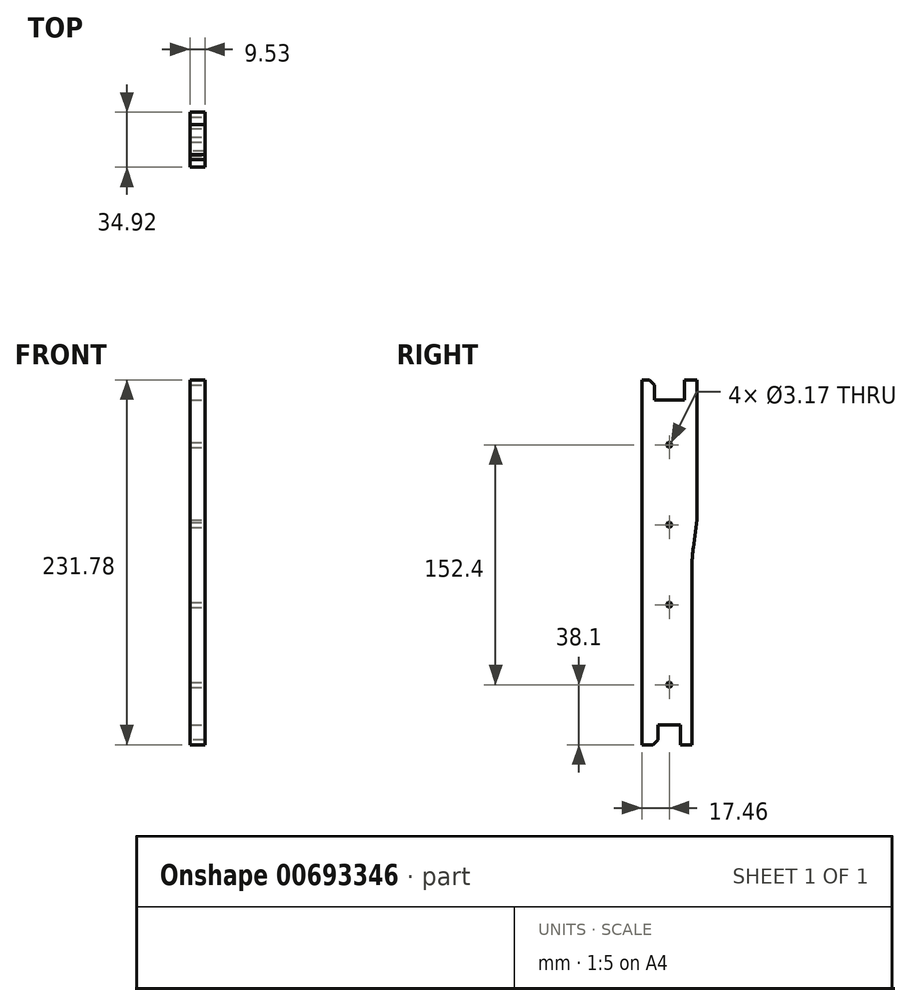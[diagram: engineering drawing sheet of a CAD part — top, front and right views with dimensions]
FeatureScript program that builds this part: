
annotation { "Feature Type Name" : "Feature", "Feature Type Description" : "" }
export const myFeature = defineFeature(function(context is Context, id is Id, definition is map)
    precondition{}
    {
        {
            var Q0;
            Q0=qCreatedBy(makeId("Right.planeOp"),FACE);
            var sketch = newSketch(context, id + "F0", { "sketchPlane" : qUnion([Q0])});
            skLineSegment(sketch, "E0.bottom", {"start": v(-17.46, 0) * mm, "end": v(17.46, 0) * mm});
            skLineSegment(sketch, "E0.top", {"start": v(-17.46, 231.78) * mm, "end": v(17.46, 231.78) * mm});
            skLineSegment(sketch, "E0.left", {"start": v(-17.46, 0) * mm, "end": v(-17.46, 231.78) * mm});
            skLineSegment(sketch, "E0.right", {"start": v(17.46, 0) * mm, "end": v(17.46, 231.78) * mm});
            skLineSegment(sketch, "E1", {"start": v(0, 0) * mm, "end": v(0, 231.78) * mm, "construction": true});
            skSolve(sketch);
        }
        {
            var Q0;
            Q0=qSketchRegion(id+"F0",true);
            extrude(context, id + "F1", {"entities" : qUnion([Q0]), "oppositeDirection" : true, "depth" : 9.52 * mm, "offsetDistance" : 25.4 * mm});
        }
        {
            var Q0;
            Q0=makeQuery(id+"F1.opExtrude","CAP_FACE",FACE,{"disambiguationData":[OSD([sQuery(id+"F0.wireOp",EDGE,"E0.bottom"),sQuery(id+"F0.wireOp",EDGE,"E0.top"),sQuery(id+"F0.wireOp",EDGE,"E0.left"),sQuery(id+"F0.wireOp",EDGE,"E0.right")])],"isStart":true});
            var sketch = newSketch(context, id + "F2", { "sketchPlane" : qUnion([Q0])});
            skLineSegment(sketch, "E2", {"start": v(14.29, 0) * mm, "end": v(14.29, 117.47) * mm});
            skLineSegment(sketch, "E3", {"start": v(14.29, 0) * mm, "end": v(17.46, 0) * mm});
            skLineSegment(sketch, "E4", {"start": v(0, 0) * mm, "end": v(0, 231.78) * mm, "construction": true});
            skLineSegment(sketch, "E5", {"start": v(14.29, 117.47) * mm, "end": v(17.46, 142.88) * mm});
            skLineSegment(sketch, "E6", {"start": v(17.46, 142.88) * mm, "end": v(17.46, 0) * mm});
            skSolve(sketch);
        }
        {
            var Q0;
            Q0=qSketchRegion(id+"F2",true);
            extrude(context, id + "F3", {"entities" : qUnion([Q0]), "operationType" : NewBodyOperationType.REMOVE, "endBound" : BoundingType.UP_TO_NEXT, "oppositeDirection" : true, "depth" : 25.4 * mm, "offsetDistance" : 25.4 * mm});
        }
        {
            var Q0;
            Q0=makeQuery(id+"F3.boolean.opBoolean","COPY",EDGE,{"derivedFrom":makeQuery(id+"F3.opExtrude","SWEPT_EDGE",EDGE,{"disambiguationData":[OSD([sQuery(id+"F2.wireOp",EDGE,"E2"),sQuery(id+"F2.wireOp",EDGE,"E5")])]})});
            var Q1;
            Q1=makeQuery(id+"F3.boolean.opBoolean","COPY",EDGE,{"derivedFrom":makeQuery(id+"F3.opExtrude","SWEPT_EDGE",EDGE,{"disambiguationData":[OSD([sQuery(id+"F0.wireOp",EDGE,"E0.right"),sQuery(id+"F2.wireOp",EDGE,"E5"),sQuery(id+"F2.wireOp",EDGE,"E6")])]})});
            fillet(context, id + "F4", {"entities" : qUnion([Q0, Q1]), "radius" : 127 * mm, "tangentPropagation" : true, "allowEdgeOverflow" : false});
        }
        {
            var Q0;
            Q0=makeQuery(id+"F1.opExtrude","CAP_FACE",FACE,{"disambiguationData":[OSD([sQuery(id+"F0.wireOp",EDGE,"E0.bottom"),sQuery(id+"F0.wireOp",EDGE,"E0.top"),sQuery(id+"F0.wireOp",EDGE,"E0.left"),sQuery(id+"F0.wireOp",EDGE,"E0.right")])],"isStart":true});
            var sketch = newSketch(context, id + "F5", { "sketchPlane" : qUnion([Q0])});
            skLineSegment(sketch, "E7", {"start": v(0, 231.78) * mm, "end": v(0, 202.75) * mm, "construction": true});
            skLineSegment(sketch, "E8.bottom", {"start": v(-9.53, 231.78) * mm, "end": v(9.53, 231.78) * mm});
            skLineSegment(sketch, "E8.top", {"start": v(-9.53, 219.08) * mm, "end": v(9.53, 219.08) * mm});
            skLineSegment(sketch, "E8.left", {"start": v(-9.53, 231.78) * mm, "end": v(-9.53, 219.08) * mm});
            skLineSegment(sketch, "E8.right", {"start": v(9.52, 231.78) * mm, "end": v(9.52, 219.08) * mm});
            skLineSegment(sketch, "E9.bottom", {"start": v(-7.14, 0) * mm, "end": v(7.14, 0) * mm});
            skLineSegment(sketch, "E9.top", {"start": v(-7.14, 12.7) * mm, "end": v(7.14, 12.7) * mm});
            skLineSegment(sketch, "E9.left", {"start": v(-7.14, 0) * mm, "end": v(-7.14, 12.7) * mm});
            skLineSegment(sketch, "E9.right", {"start": v(7.14, 0) * mm, "end": v(7.14, 12.7) * mm});
            skSolve(sketch);
        }
        {
            var Q0;
            Q0=qSketchRegion(id+"F5",true);
            extrude(context, id + "F6", {"entities" : qUnion([Q0]), "operationType" : NewBodyOperationType.REMOVE, "endBound" : BoundingType.UP_TO_NEXT, "oppositeDirection" : true, "depth" : 25.4 * mm, "offsetDistance" : 25.4 * mm});
        }
        {
            var Q0;
            Q0=makeQuery(id+"F6.boolean.opBoolean","COPY",EDGE,{"derivedFrom":makeQuery(id+"F6.opExtrude","SWEPT_EDGE",EDGE,{"disambiguationData":[OSD([sQuery(id+"F0.wireOp",EDGE,"E0.top"),sQuery(id+"F5.wireOp",EDGE,"E8.bottom"),sQuery(id+"F5.wireOp",EDGE,"E8.left")])]})});
            var Q1;
            Q1=makeQuery(id+"F6.boolean.opBoolean","COPY",EDGE,{"derivedFrom":makeQuery(id+"F6.opExtrude","SWEPT_EDGE",EDGE,{"disambiguationData":[OSD([sQuery(id+"F0.wireOp",EDGE,"E0.top"),sQuery(id+"F5.wireOp",EDGE,"E8.bottom"),sQuery(id+"F5.wireOp",EDGE,"E8.right")])]})});
            var Q2;
            Q2=makeQuery(id+"F6.boolean.opBoolean","COPY",EDGE,{"derivedFrom":makeQuery(id+"F6.opExtrude","SWEPT_EDGE",EDGE,{"disambiguationData":[OSD([sQuery(id+"F0.wireOp",EDGE,"E0.bottom"),sQuery(id+"F5.wireOp",EDGE,"E9.bottom"),sQuery(id+"F5.wireOp",EDGE,"E9.left")])]})});
            var Q3;
            Q3=makeQuery(id+"F6.boolean.opBoolean","COPY",EDGE,{"derivedFrom":makeQuery(id+"F6.opExtrude","SWEPT_EDGE",EDGE,{"disambiguationData":[OSD([sQuery(id+"F0.wireOp",EDGE,"E0.bottom"),sQuery(id+"F5.wireOp",EDGE,"E9.bottom"),sQuery(id+"F5.wireOp",EDGE,"E9.right")])]})});
            chamfer(context, id + "F7", {"entities" : qUnion([Q0, Q1, Q2, Q3]), "width" : 3.17 * mm, "tangentPropagation" : true});
        }
        {
            var Q0;
            Q0=makeQuery(id+"F1.opExtrude","CAP_FACE",FACE,{"disambiguationData":[OSD([sQuery(id+"F0.wireOp",EDGE,"E0.bottom"),sQuery(id+"F0.wireOp",EDGE,"E0.top"),sQuery(id+"F0.wireOp",EDGE,"E0.left"),sQuery(id+"F0.wireOp",EDGE,"E0.right")])],"isStart":true});
            var sketch = newSketch(context, id + "F8", { "sketchPlane" : qUnion([Q0])});
            skLineSegment(sketch, "E10", {"start": v(0, 219.08) * mm, "end": v(0, 12.7) * mm, "construction": true});
            skPoint(sketch, "E11", {"position": v(0, 190.5) * mm});
            skPoint(sketch, "E12", {"position": v(0, 139.7) * mm});
            skPoint(sketch, "E13", {"position": v(0, 88.9) * mm});
            skPoint(sketch, "E14", {"position": v(0, 38.1) * mm});
            skSolve(sketch);
        }
        {
            var Q0;
            Q0=sQuery(id+"F8.wireOp",VERTEX,"E12");
            var Q1;
            Q1=sQuery(id+"F8.wireOp",VERTEX,"E13");
            var Q2;
            Q2=sQuery(id+"F8.wireOp",VERTEX,"E11");
            var Q3;
            Q3=sQuery(id+"F8.wireOp",VERTEX,"E14");
            var Q4;
            Q4=makeQuery(id+"F1.opExtrude","SWEPT_BODY",BODY,{"disambiguationData":[OSD([sQuery(id+"F0.wireOp",EDGE,"E0.bottom"),sQuery(id+"F0.wireOp",EDGE,"E0.top"),sQuery(id+"F0.wireOp",EDGE,"E0.left"),sQuery(id+"F0.wireOp",EDGE,"E0.right")])]});
            hole(context, id + "F9", {"style" : HoleStyle.SIMPLE, "endStyle" : HoleEndStyle.THROUGH, "holeDiameter" : 3.17 * mm, "majorDiameter" : 6.35 * mm, "isTappedThrough" : true, "tappedDepth" : 12.7 * mm, "tapClearance" : 3, "locations" : qUnion([Q0, Q1, Q2, Q3]), "scope" : qUnion([Q4])});
        }
    });
